# Revit family: Accessory-Flush_Actuator_Plate-KOHLER-Lynk-K-75890_1
name_source: partatom
category: Specialty Equipment
revit_build: Autodesk Revit 2017 (Build: 20160225_1515(x64)
units: mm (PartAtom-declared; Revit-internal decimal feet)

## family parameters
Cut with Voids When Loaded = No
Host = Face
OmniClass Number = 23.31.25.00
OmniClass Title = Toilet and Bath Specialties
Part Type = Normal
Room Calculation Point = No
Round Connector Dimension = Use Diameter
Shared = No

## types (5) — shared parameters
ADA Compliant = No
Assembly Code = C1030200
Date Modified = 11/10/2020
Default Elevation = 42"
Description = flush actuator plate for 2 inchx 4 inch in-wall tank and carrier system
Height = 6 5/16"
Length = 7/16"
Manufacturer = KOHLER Co.
Master Format 2014 = 10 28 00
Master Format 2014 Name = Toilet, Bath, and Laundry Accessories
Material = Plastic
Product Documentation Link = https://www.us.kohler.com
Product Name = Lynk
Product Page URL = http://www.us.kohler.com
URL = https://www.us.kohler.com
WaterSense Certified = No
Width = 8 7/8"

## per-type parameters (varying)
| type | Finish | Model | Type |
| 0-White | Kohler-Plastic-0-White | K-75890-0 | 1 |
| CP-Polished Chrome | Kohler-Plastic-CP-Polished_Chrome | K-75890-CP | 2 |
| AF-Vibrant French Gold | KOHLER-Plastic-AF-Vibrant_French_Gold | K-75890-AF | 3 |
| BN-Vibrant Brushed Nickel | KOHLER-Plastic-BN-Vibrant_Brushed_Nickel | K-75890-BN | 4 |
| 7-Black Black | Kohler-Plastic-7-Black_Black | K-75890-7 | 5 |

## geometry (parser evidence)
native form markers: Sweep x6
no freeform markers — native parametric forms only
